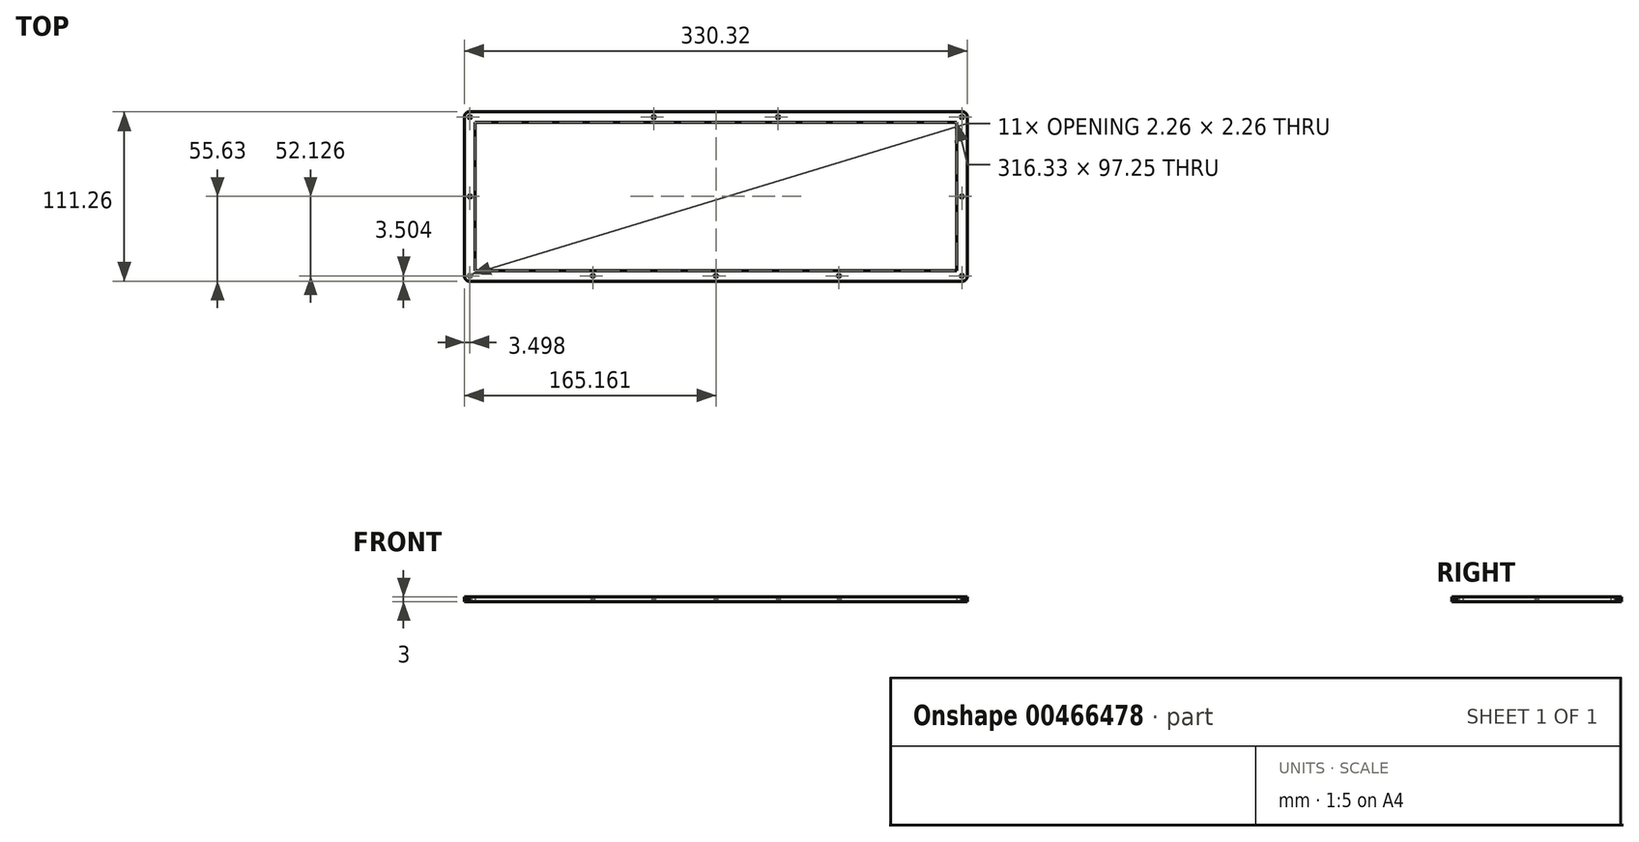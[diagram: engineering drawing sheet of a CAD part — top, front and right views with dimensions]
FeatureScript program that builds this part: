
annotation { "Feature Type Name" : "Feature", "Feature Type Description" : "" }
export const myFeature = defineFeature(function(context is Context, id is Id, definition is map)
    precondition{}
    {
        {
            var Q0;
            Q0=qCreatedBy(makeId("Top.planeOp"),FACE);
            var sketch = newSketch(context, id + "F0", { "sketchPlane" : qUnion([Q0])});
            skLineSegment(sketch, "E0", {"start": v(162.16, 55.62) * mm, "end": v(162.4, 55.62) * mm});
            skLineSegment(sketch, "E1", {"start": v(162.4, 55.62) * mm, "end": v(162.63, 55.59) * mm});
            skLineSegment(sketch, "E2", {"start": v(162.63, 55.59) * mm, "end": v(162.86, 55.54) * mm});
            skLineSegment(sketch, "E3", {"start": v(162.86, 55.54) * mm, "end": v(163.1, 55.48) * mm});
            skLineSegment(sketch, "E4", {"start": v(163.1, 55.48) * mm, "end": v(163.31, 55.4) * mm});
            skLineSegment(sketch, "E5", {"start": v(163.31, 55.4) * mm, "end": v(163.53, 55.3) * mm});
            skLineSegment(sketch, "E6", {"start": v(163.53, 55.3) * mm, "end": v(163.73, 55.18) * mm});
            skLineSegment(sketch, "E7", {"start": v(163.73, 55.18) * mm, "end": v(163.93, 55.05) * mm});
            skLineSegment(sketch, "E8", {"start": v(163.93, 55.05) * mm, "end": v(164.11, 54.9) * mm});
            skLineSegment(sketch, "E9", {"start": v(164.11, 54.9) * mm, "end": v(164.29, 54.75) * mm});
            skLineSegment(sketch, "E10", {"start": v(164.29, 54.75) * mm, "end": v(164.45, 54.57) * mm});
            skLineSegment(sketch, "E11", {"start": v(164.45, 54.57) * mm, "end": v(164.6, 54.39) * mm});
            skLineSegment(sketch, "E12", {"start": v(164.6, 54.39) * mm, "end": v(164.72, 54.2) * mm});
            skLineSegment(sketch, "E13", {"start": v(164.72, 54.2) * mm, "end": v(164.84, 53.99) * mm});
            skLineSegment(sketch, "E14", {"start": v(164.84, 53.99) * mm, "end": v(164.93, 53.77) * mm});
            skLineSegment(sketch, "E15", {"start": v(164.93, 53.77) * mm, "end": v(165.02, 53.55) * mm});
            skLineSegment(sketch, "E16", {"start": v(165.02, 53.55) * mm, "end": v(165.08, 53.33) * mm});
            skLineSegment(sketch, "E17", {"start": v(165.08, 53.33) * mm, "end": v(165.13, 53.1) * mm});
            skLineSegment(sketch, "E18", {"start": v(165.13, 53.1) * mm, "end": v(165.15, 52.86) * mm});
            skLineSegment(sketch, "E19", {"start": v(165.15, 52.86) * mm, "end": v(165.16, 52.62) * mm});
            skLineSegment(sketch, "E20", {"start": v(165.16, 52.62) * mm, "end": v(165.16, -52.63) * mm});
            skLineSegment(sketch, "E21", {"start": v(165.16, -52.63) * mm, "end": v(165.15, -52.86) * mm});
            skLineSegment(sketch, "E22", {"start": v(165.15, -52.86) * mm, "end": v(165.13, -53.1) * mm});
            skLineSegment(sketch, "E23", {"start": v(165.13, -53.1) * mm, "end": v(165.08, -53.33) * mm});
            skLineSegment(sketch, "E24", {"start": v(165.08, -53.33) * mm, "end": v(165.02, -53.55) * mm});
            skLineSegment(sketch, "E25", {"start": v(165.02, -53.55) * mm, "end": v(164.93, -53.77) * mm});
            skLineSegment(sketch, "E26", {"start": v(164.93, -53.77) * mm, "end": v(164.84, -53.99) * mm});
            skLineSegment(sketch, "E27", {"start": v(164.84, -53.99) * mm, "end": v(164.72, -54.2) * mm});
            skLineSegment(sketch, "E28", {"start": v(164.72, -54.2) * mm, "end": v(164.6, -54.39) * mm});
            skLineSegment(sketch, "E29", {"start": v(164.6, -54.39) * mm, "end": v(164.45, -54.57) * mm});
            skLineSegment(sketch, "E30", {"start": v(164.45, -54.57) * mm, "end": v(164.29, -54.75) * mm});
            skLineSegment(sketch, "E31", {"start": v(164.29, -54.75) * mm, "end": v(164.11, -54.9) * mm});
            skLineSegment(sketch, "E32", {"start": v(164.11, -54.9) * mm, "end": v(163.93, -55.05) * mm});
            skLineSegment(sketch, "E33", {"start": v(163.93, -55.05) * mm, "end": v(163.73, -55.18) * mm});
            skLineSegment(sketch, "E34", {"start": v(163.73, -55.18) * mm, "end": v(163.53, -55.3) * mm});
            skLineSegment(sketch, "E35", {"start": v(163.53, -55.3) * mm, "end": v(163.31, -55.4) * mm});
            skLineSegment(sketch, "E36", {"start": v(163.31, -55.4) * mm, "end": v(163.1, -55.48) * mm});
            skLineSegment(sketch, "E37", {"start": v(163.1, -55.48) * mm, "end": v(162.86, -55.54) * mm});
            skLineSegment(sketch, "E38", {"start": v(162.86, -55.54) * mm, "end": v(162.63, -55.59) * mm});
            skLineSegment(sketch, "E39", {"start": v(162.63, -55.59) * mm, "end": v(162.4, -55.62) * mm});
            skLineSegment(sketch, "E40", {"start": v(162.4, -55.62) * mm, "end": v(162.16, -55.63) * mm});
            skLineSegment(sketch, "E41", {"start": v(162.16, -55.63) * mm, "end": v(-162.16, -55.63) * mm});
            skLineSegment(sketch, "E42", {"start": v(-162.16, -55.63) * mm, "end": v(-162.4, -55.62) * mm});
            skLineSegment(sketch, "E43", {"start": v(-162.4, -55.62) * mm, "end": v(-162.63, -55.59) * mm});
            skLineSegment(sketch, "E44", {"start": v(-162.63, -55.59) * mm, "end": v(-162.86, -55.54) * mm});
            skLineSegment(sketch, "E45", {"start": v(-162.86, -55.54) * mm, "end": v(-163.09, -55.48) * mm});
            skLineSegment(sketch, "E46", {"start": v(-163.09, -55.48) * mm, "end": v(-163.31, -55.4) * mm});
            skLineSegment(sketch, "E47", {"start": v(-163.31, -55.4) * mm, "end": v(-163.52, -55.3) * mm});
            skLineSegment(sketch, "E48", {"start": v(-163.52, -55.3) * mm, "end": v(-163.73, -55.18) * mm});
            skLineSegment(sketch, "E49", {"start": v(-163.73, -55.18) * mm, "end": v(-163.93, -55.05) * mm});
            skLineSegment(sketch, "E50", {"start": v(-163.93, -55.05) * mm, "end": v(-164.11, -54.9) * mm});
            skLineSegment(sketch, "E51", {"start": v(-164.11, -54.9) * mm, "end": v(-164.28, -54.75) * mm});
            skLineSegment(sketch, "E52", {"start": v(-164.28, -54.75) * mm, "end": v(-164.44, -54.57) * mm});
            skLineSegment(sketch, "E53", {"start": v(-164.44, -54.57) * mm, "end": v(-164.6, -54.39) * mm});
            skLineSegment(sketch, "E54", {"start": v(-164.6, -54.39) * mm, "end": v(-164.72, -54.2) * mm});
            skLineSegment(sketch, "E55", {"start": v(-164.72, -54.2) * mm, "end": v(-164.84, -53.99) * mm});
            skLineSegment(sketch, "E56", {"start": v(-164.84, -53.99) * mm, "end": v(-164.93, -53.77) * mm});
            skLineSegment(sketch, "E57", {"start": v(-164.93, -53.77) * mm, "end": v(-165.02, -53.55) * mm});
            skLineSegment(sketch, "E58", {"start": v(-165.02, -53.55) * mm, "end": v(-165.08, -53.33) * mm});
            skLineSegment(sketch, "E59", {"start": v(-165.08, -53.33) * mm, "end": v(-165.13, -53.1) * mm});
            skLineSegment(sketch, "E60", {"start": v(-165.13, -53.1) * mm, "end": v(-165.15, -52.86) * mm});
            skLineSegment(sketch, "E61", {"start": v(-165.15, -52.86) * mm, "end": v(-165.16, -52.63) * mm});
            skLineSegment(sketch, "E62", {"start": v(-165.16, -52.63) * mm, "end": v(-165.16, 52.62) * mm});
            skLineSegment(sketch, "E63", {"start": v(-165.16, 52.62) * mm, "end": v(-165.15, 52.86) * mm});
            skLineSegment(sketch, "E64", {"start": v(-165.15, 52.86) * mm, "end": v(-165.13, 53.1) * mm});
            skLineSegment(sketch, "E65", {"start": v(-165.13, 53.1) * mm, "end": v(-165.08, 53.33) * mm});
            skLineSegment(sketch, "E66", {"start": v(-165.08, 53.33) * mm, "end": v(-165.02, 53.55) * mm});
            skLineSegment(sketch, "E67", {"start": v(-165.02, 53.55) * mm, "end": v(-164.93, 53.77) * mm});
            skLineSegment(sketch, "E68", {"start": v(-164.93, 53.77) * mm, "end": v(-164.84, 53.99) * mm});
            skLineSegment(sketch, "E69", {"start": v(-164.84, 53.99) * mm, "end": v(-164.72, 54.2) * mm});
            skLineSegment(sketch, "E70", {"start": v(-164.72, 54.2) * mm, "end": v(-164.6, 54.39) * mm});
            skLineSegment(sketch, "E71", {"start": v(-164.6, 54.39) * mm, "end": v(-164.44, 54.57) * mm});
            skLineSegment(sketch, "E72", {"start": v(-164.44, 54.57) * mm, "end": v(-164.28, 54.75) * mm});
            skLineSegment(sketch, "E73", {"start": v(-164.28, 54.75) * mm, "end": v(-164.11, 54.9) * mm});
            skLineSegment(sketch, "E74", {"start": v(-164.11, 54.9) * mm, "end": v(-163.93, 55.05) * mm});
            skLineSegment(sketch, "E75", {"start": v(-163.93, 55.05) * mm, "end": v(-163.73, 55.18) * mm});
            skLineSegment(sketch, "E76", {"start": v(-163.73, 55.18) * mm, "end": v(-163.52, 55.3) * mm});
            skLineSegment(sketch, "E77", {"start": v(-163.52, 55.3) * mm, "end": v(-163.31, 55.4) * mm});
            skLineSegment(sketch, "E78", {"start": v(-163.31, 55.4) * mm, "end": v(-163.09, 55.48) * mm});
            skLineSegment(sketch, "E79", {"start": v(-163.09, 55.48) * mm, "end": v(-162.86, 55.54) * mm});
            skLineSegment(sketch, "E80", {"start": v(-162.86, 55.54) * mm, "end": v(-162.63, 55.59) * mm});
            skLineSegment(sketch, "E81", {"start": v(-162.63, 55.59) * mm, "end": v(-162.4, 55.62) * mm});
            skLineSegment(sketch, "E82", {"start": v(-162.4, 55.62) * mm, "end": v(-162.16, 55.63) * mm});
            skLineSegment(sketch, "E83", {"start": v(-162.16, 55.63) * mm, "end": v(162.16, 55.62) * mm});
            skLineSegment(sketch, "E84", {"start": v(161.31, -51.05) * mm, "end": v(161, -51.21) * mm});
            skLineSegment(sketch, "E85", {"start": v(161, -51.21) * mm, "end": v(160.75, -51.46) * mm});
            skLineSegment(sketch, "E86", {"start": v(160.75, -51.46) * mm, "end": v(160.59, -51.78) * mm});
            skLineSegment(sketch, "E87", {"start": v(160.59, -51.78) * mm, "end": v(160.53, -52.13) * mm});
            skLineSegment(sketch, "E88", {"start": v(160.53, -52.13) * mm, "end": v(160.59, -52.48) * mm});
            skLineSegment(sketch, "E89", {"start": v(160.59, -52.48) * mm, "end": v(160.75, -52.79) * mm});
            skLineSegment(sketch, "E90", {"start": v(160.75, -52.79) * mm, "end": v(161, -53.04) * mm});
            skLineSegment(sketch, "E91", {"start": v(161, -53.04) * mm, "end": v(161.31, -53.2) * mm});
            skLineSegment(sketch, "E92", {"start": v(161.31, -53.2) * mm, "end": v(161.66, -53.26) * mm});
            skLineSegment(sketch, "E93", {"start": v(161.66, -53.26) * mm, "end": v(162.01, -53.2) * mm});
            skLineSegment(sketch, "E94", {"start": v(162.01, -53.2) * mm, "end": v(162.33, -53.04) * mm});
            skLineSegment(sketch, "E95", {"start": v(162.33, -53.04) * mm, "end": v(162.58, -52.79) * mm});
            skLineSegment(sketch, "E96", {"start": v(162.58, -52.79) * mm, "end": v(162.74, -52.48) * mm});
            skLineSegment(sketch, "E97", {"start": v(162.74, -52.48) * mm, "end": v(162.8, -52.13) * mm});
            skLineSegment(sketch, "E98", {"start": v(162.8, -52.13) * mm, "end": v(162.74, -51.78) * mm});
            skLineSegment(sketch, "E99", {"start": v(162.74, -51.78) * mm, "end": v(162.58, -51.46) * mm});
            skLineSegment(sketch, "E100", {"start": v(162.58, -51.46) * mm, "end": v(162.33, -51.21) * mm});
            skLineSegment(sketch, "E101", {"start": v(162.33, -51.21) * mm, "end": v(162.01, -51.05) * mm});
            skLineSegment(sketch, "E102", {"start": v(162.01, -51.05) * mm, "end": v(161.66, -51) * mm});
            skLineSegment(sketch, "E103", {"start": v(161.66, -51) * mm, "end": v(161.31, -51.05) * mm});
            skLineSegment(sketch, "E104", {"start": v(80.48, -51.05) * mm, "end": v(80.17, -51.21) * mm});
            skLineSegment(sketch, "E105", {"start": v(80.17, -51.21) * mm, "end": v(79.92, -51.46) * mm});
            skLineSegment(sketch, "E106", {"start": v(79.92, -51.46) * mm, "end": v(79.76, -51.78) * mm});
            skLineSegment(sketch, "E107", {"start": v(79.76, -51.78) * mm, "end": v(79.7, -52.13) * mm});
            skLineSegment(sketch, "E108", {"start": v(79.7, -52.13) * mm, "end": v(79.76, -52.48) * mm});
            skLineSegment(sketch, "E109", {"start": v(79.76, -52.48) * mm, "end": v(79.92, -52.79) * mm});
            skLineSegment(sketch, "E110", {"start": v(79.92, -52.79) * mm, "end": v(80.17, -53.04) * mm});
            skLineSegment(sketch, "E111", {"start": v(80.17, -53.04) * mm, "end": v(80.48, -53.2) * mm});
            skLineSegment(sketch, "E112", {"start": v(80.48, -53.2) * mm, "end": v(80.83, -53.26) * mm});
            skLineSegment(sketch, "E113", {"start": v(80.83, -53.26) * mm, "end": v(81.18, -53.2) * mm});
            skLineSegment(sketch, "E114", {"start": v(81.18, -53.2) * mm, "end": v(81.5, -53.04) * mm});
            skLineSegment(sketch, "E115", {"start": v(81.5, -53.04) * mm, "end": v(81.75, -52.79) * mm});
            skLineSegment(sketch, "E116", {"start": v(81.75, -52.79) * mm, "end": v(81.9, -52.48) * mm});
            skLineSegment(sketch, "E117", {"start": v(81.9, -52.48) * mm, "end": v(81.96, -52.13) * mm});
            skLineSegment(sketch, "E118", {"start": v(81.96, -52.13) * mm, "end": v(81.9, -51.78) * mm});
            skLineSegment(sketch, "E119", {"start": v(81.9, -51.78) * mm, "end": v(81.75, -51.46) * mm});
            skLineSegment(sketch, "E120", {"start": v(81.75, -51.46) * mm, "end": v(81.5, -51.21) * mm});
            skLineSegment(sketch, "E121", {"start": v(81.5, -51.21) * mm, "end": v(81.18, -51.05) * mm});
            skLineSegment(sketch, "E122", {"start": v(81.18, -51.05) * mm, "end": v(80.83, -51) * mm});
            skLineSegment(sketch, "E123", {"start": v(80.83, -51) * mm, "end": v(80.48, -51.05) * mm});
            skLineSegment(sketch, "E124", {"start": v(-0.35, -51.05) * mm, "end": v(-0.66, -51.21) * mm});
            skLineSegment(sketch, "E125", {"start": v(-0.66, -51.21) * mm, "end": v(-0.91, -51.46) * mm});
            skLineSegment(sketch, "E126", {"start": v(-0.91, -51.46) * mm, "end": v(-1.07, -51.78) * mm});
            skLineSegment(sketch, "E127", {"start": v(-1.07, -51.78) * mm, "end": v(-1.13, -52.13) * mm});
            skLineSegment(sketch, "E128", {"start": v(-1.13, -52.13) * mm, "end": v(-1.07, -52.48) * mm});
            skLineSegment(sketch, "E129", {"start": v(-1.07, -52.48) * mm, "end": v(-0.91, -52.79) * mm});
            skLineSegment(sketch, "E130", {"start": v(-0.91, -52.79) * mm, "end": v(-0.66, -53.04) * mm});
            skLineSegment(sketch, "E131", {"start": v(-0.66, -53.04) * mm, "end": v(-0.35, -53.2) * mm});
            skLineSegment(sketch, "E132", {"start": v(-0.35, -53.2) * mm, "end": v(0, -53.26) * mm});
            skLineSegment(sketch, "E133", {"start": v(0, -53.26) * mm, "end": v(0.35, -53.2) * mm});
            skLineSegment(sketch, "E134", {"start": v(0.35, -53.2) * mm, "end": v(0.67, -53.04) * mm});
            skLineSegment(sketch, "E135", {"start": v(0.67, -53.04) * mm, "end": v(0.92, -52.79) * mm});
            skLineSegment(sketch, "E136", {"start": v(0.92, -52.79) * mm, "end": v(1.07, -52.48) * mm});
            skLineSegment(sketch, "E137", {"start": v(1.07, -52.48) * mm, "end": v(1.13, -52.13) * mm});
            skLineSegment(sketch, "E138", {"start": v(1.13, -52.13) * mm, "end": v(1.07, -51.78) * mm});
            skLineSegment(sketch, "E139", {"start": v(1.07, -51.78) * mm, "end": v(0.92, -51.46) * mm});
            skLineSegment(sketch, "E140", {"start": v(0.92, -51.46) * mm, "end": v(0.67, -51.21) * mm});
            skLineSegment(sketch, "E141", {"start": v(0.67, -51.21) * mm, "end": v(0.35, -51.05) * mm});
            skLineSegment(sketch, "E142", {"start": v(0.35, -51.05) * mm, "end": v(0, -51) * mm});
            skLineSegment(sketch, "E143", {"start": v(0, -51) * mm, "end": v(-0.35, -51.05) * mm});
            skLineSegment(sketch, "E144", {"start": v(-81.18, -51.05) * mm, "end": v(-81.5, -51.21) * mm});
            skLineSegment(sketch, "E145", {"start": v(-81.5, -51.21) * mm, "end": v(-81.75, -51.46) * mm});
            skLineSegment(sketch, "E146", {"start": v(-81.75, -51.46) * mm, "end": v(-81.9, -51.78) * mm});
            skLineSegment(sketch, "E147", {"start": v(-81.9, -51.78) * mm, "end": v(-81.96, -52.13) * mm});
            skLineSegment(sketch, "E148", {"start": v(-81.96, -52.13) * mm, "end": v(-81.9, -52.48) * mm});
            skLineSegment(sketch, "E149", {"start": v(-81.9, -52.48) * mm, "end": v(-81.75, -52.79) * mm});
            skLineSegment(sketch, "E150", {"start": v(-81.75, -52.79) * mm, "end": v(-81.5, -53.04) * mm});
            skLineSegment(sketch, "E151", {"start": v(-81.5, -53.04) * mm, "end": v(-81.18, -53.2) * mm});
            skLineSegment(sketch, "E152", {"start": v(-81.18, -53.2) * mm, "end": v(-80.83, -53.26) * mm});
            skLineSegment(sketch, "E153", {"start": v(-80.83, -53.26) * mm, "end": v(-80.48, -53.2) * mm});
            skLineSegment(sketch, "E154", {"start": v(-80.48, -53.2) * mm, "end": v(-80.17, -53.04) * mm});
            skLineSegment(sketch, "E155", {"start": v(-80.17, -53.04) * mm, "end": v(-79.92, -52.79) * mm});
            skLineSegment(sketch, "E156", {"start": v(-79.92, -52.79) * mm, "end": v(-79.76, -52.48) * mm});
            skLineSegment(sketch, "E157", {"start": v(-79.76, -52.48) * mm, "end": v(-79.7, -52.13) * mm});
            skLineSegment(sketch, "E158", {"start": v(-79.7, -52.13) * mm, "end": v(-79.76, -51.78) * mm});
            skLineSegment(sketch, "E159", {"start": v(-79.76, -51.78) * mm, "end": v(-79.92, -51.46) * mm});
            skLineSegment(sketch, "E160", {"start": v(-79.92, -51.46) * mm, "end": v(-80.17, -51.21) * mm});
            skLineSegment(sketch, "E161", {"start": v(-80.17, -51.21) * mm, "end": v(-80.48, -51.05) * mm});
            skLineSegment(sketch, "E162", {"start": v(-80.48, -51.05) * mm, "end": v(-80.83, -51) * mm});
            skLineSegment(sketch, "E163", {"start": v(-80.83, -51) * mm, "end": v(-81.18, -51.05) * mm});
            skLineSegment(sketch, "E164", {"start": v(-162.01, -51.05) * mm, "end": v(-162.33, -51.21) * mm});
            skLineSegment(sketch, "E165", {"start": v(-162.33, -51.21) * mm, "end": v(-162.58, -51.46) * mm});
            skLineSegment(sketch, "E166", {"start": v(-162.58, -51.46) * mm, "end": v(-162.74, -51.78) * mm});
            skLineSegment(sketch, "E167", {"start": v(-162.74, -51.78) * mm, "end": v(-162.8, -52.13) * mm});
            skLineSegment(sketch, "E168", {"start": v(-162.8, -52.13) * mm, "end": v(-162.74, -52.48) * mm});
            skLineSegment(sketch, "E169", {"start": v(-162.74, -52.48) * mm, "end": v(-162.58, -52.79) * mm});
            skLineSegment(sketch, "E170", {"start": v(-162.58, -52.79) * mm, "end": v(-162.33, -53.04) * mm});
            skLineSegment(sketch, "E171", {"start": v(-162.33, -53.04) * mm, "end": v(-162.01, -53.2) * mm});
            skLineSegment(sketch, "E172", {"start": v(-162.01, -53.2) * mm, "end": v(-161.66, -53.26) * mm});
            skLineSegment(sketch, "E173", {"start": v(-161.66, -53.26) * mm, "end": v(-161.31, -53.2) * mm});
            skLineSegment(sketch, "E174", {"start": v(-161.31, -53.2) * mm, "end": v(-161, -53.04) * mm});
            skLineSegment(sketch, "E175", {"start": v(-161, -53.04) * mm, "end": v(-160.75, -52.79) * mm});
            skLineSegment(sketch, "E176", {"start": v(-160.75, -52.79) * mm, "end": v(-160.59, -52.48) * mm});
            skLineSegment(sketch, "E177", {"start": v(-160.59, -52.48) * mm, "end": v(-160.53, -52.13) * mm});
            skLineSegment(sketch, "E178", {"start": v(-160.53, -52.13) * mm, "end": v(-160.59, -51.78) * mm});
            skLineSegment(sketch, "E179", {"start": v(-160.59, -51.78) * mm, "end": v(-160.75, -51.46) * mm});
            skLineSegment(sketch, "E180", {"start": v(-160.75, -51.46) * mm, "end": v(-161, -51.21) * mm});
            skLineSegment(sketch, "E181", {"start": v(-161, -51.21) * mm, "end": v(-161.31, -51.05) * mm});
            skLineSegment(sketch, "E182", {"start": v(-161.31, -51.05) * mm, "end": v(-161.66, -51) * mm});
            skLineSegment(sketch, "E183", {"start": v(-161.66, -51) * mm, "end": v(-162.01, -51.05) * mm});
            skLineSegment(sketch, "E184", {"start": v(-158.16, 48.62) * mm, "end": v(158.16, 48.62) * mm});
            skLineSegment(sketch, "E185", {"start": v(158.16, 48.62) * mm, "end": v(158.16, -48.63) * mm});
            skLineSegment(sketch, "E186", {"start": v(158.16, -48.63) * mm, "end": v(-158.16, -48.63) * mm});
            skLineSegment(sketch, "E187", {"start": v(-158.16, -48.63) * mm, "end": v(-158.16, 48.62) * mm});
            skLineSegment(sketch, "E188", {"start": v(161.31, 1.08) * mm, "end": v(161, 0.91) * mm});
            skLineSegment(sketch, "E189", {"start": v(161, 0.91) * mm, "end": v(160.75, 0.66) * mm});
            skLineSegment(sketch, "E190", {"start": v(160.75, 0.66) * mm, "end": v(160.59, 0.35) * mm});
            skLineSegment(sketch, "E191", {"start": v(160.59, 0.35) * mm, "end": v(160.53, 0) * mm});
            skLineSegment(sketch, "E192", {"start": v(160.53, 0) * mm, "end": v(160.59, -0.35) * mm});
            skLineSegment(sketch, "E193", {"start": v(160.59, -0.35) * mm, "end": v(160.75, -0.66) * mm});
            skLineSegment(sketch, "E194", {"start": v(160.75, -0.66) * mm, "end": v(161, -0.91) * mm});
            skLineSegment(sketch, "E195", {"start": v(161, -0.91) * mm, "end": v(161.31, -1.07) * mm});
            skLineSegment(sketch, "E196", {"start": v(161.31, -1.07) * mm, "end": v(161.66, -1.13) * mm});
            skLineSegment(sketch, "E197", {"start": v(161.66, -1.13) * mm, "end": v(162.01, -1.07) * mm});
            skLineSegment(sketch, "E198", {"start": v(162.01, -1.07) * mm, "end": v(162.33, -0.91) * mm});
            skLineSegment(sketch, "E199", {"start": v(162.33, -0.91) * mm, "end": v(162.58, -0.66) * mm});
            skLineSegment(sketch, "E200", {"start": v(162.58, -0.66) * mm, "end": v(162.74, -0.35) * mm});
            skLineSegment(sketch, "E201", {"start": v(162.74, -0.35) * mm, "end": v(162.8, 0) * mm});
            skLineSegment(sketch, "E202", {"start": v(162.8, 0) * mm, "end": v(162.74, 0.35) * mm});
            skLineSegment(sketch, "E203", {"start": v(162.74, 0.35) * mm, "end": v(162.58, 0.66) * mm});
            skLineSegment(sketch, "E204", {"start": v(162.58, 0.66) * mm, "end": v(162.33, 0.91) * mm});
            skLineSegment(sketch, "E205", {"start": v(162.33, 0.91) * mm, "end": v(162.01, 1.08) * mm});
            skLineSegment(sketch, "E206", {"start": v(162.01, 1.08) * mm, "end": v(161.66, 1.13) * mm});
            skLineSegment(sketch, "E207", {"start": v(161.66, 1.13) * mm, "end": v(161.31, 1.08) * mm});
            skLineSegment(sketch, "E208", {"start": v(-162.01, 1.08) * mm, "end": v(-162.33, 0.91) * mm});
            skLineSegment(sketch, "E209", {"start": v(-162.33, 0.91) * mm, "end": v(-162.58, 0.66) * mm});
            skLineSegment(sketch, "E210", {"start": v(-162.58, 0.66) * mm, "end": v(-162.74, 0.35) * mm});
            skLineSegment(sketch, "E211", {"start": v(-162.74, 0.35) * mm, "end": v(-162.8, 0) * mm});
            skLineSegment(sketch, "E212", {"start": v(-162.8, 0) * mm, "end": v(-162.74, -0.35) * mm});
            skLineSegment(sketch, "E213", {"start": v(-162.74, -0.35) * mm, "end": v(-162.58, -0.66) * mm});
            skLineSegment(sketch, "E214", {"start": v(-162.58, -0.66) * mm, "end": v(-162.33, -0.91) * mm});
            skLineSegment(sketch, "E215", {"start": v(-162.33, -0.91) * mm, "end": v(-162.01, -1.07) * mm});
            skLineSegment(sketch, "E216", {"start": v(-162.01, -1.07) * mm, "end": v(-161.66, -1.13) * mm});
            skLineSegment(sketch, "E217", {"start": v(-161.66, -1.13) * mm, "end": v(-161.31, -1.07) * mm});
            skLineSegment(sketch, "E218", {"start": v(-161.31, -1.07) * mm, "end": v(-161, -0.91) * mm});
            skLineSegment(sketch, "E219", {"start": v(-161, -0.91) * mm, "end": v(-160.75, -0.66) * mm});
            skLineSegment(sketch, "E220", {"start": v(-160.75, -0.66) * mm, "end": v(-160.59, -0.35) * mm});
            skLineSegment(sketch, "E221", {"start": v(-160.59, -0.35) * mm, "end": v(-160.53, 0) * mm});
            skLineSegment(sketch, "E222", {"start": v(-160.53, 0) * mm, "end": v(-160.59, 0.35) * mm});
            skLineSegment(sketch, "E223", {"start": v(-160.59, 0.35) * mm, "end": v(-160.75, 0.66) * mm});
            skLineSegment(sketch, "E224", {"start": v(-160.75, 0.66) * mm, "end": v(-161, 0.91) * mm});
            skLineSegment(sketch, "E225", {"start": v(-161, 0.91) * mm, "end": v(-161.31, 1.08) * mm});
            skLineSegment(sketch, "E226", {"start": v(-161.31, 1.08) * mm, "end": v(-161.66, 1.13) * mm});
            skLineSegment(sketch, "E227", {"start": v(-161.66, 1.13) * mm, "end": v(-162.01, 1.08) * mm});
            skLineSegment(sketch, "E228", {"start": v(-41.18, 53.2) * mm, "end": v(-41.5, 53.04) * mm});
            skLineSegment(sketch, "E229", {"start": v(-41.5, 53.04) * mm, "end": v(-41.75, 52.8) * mm});
            skLineSegment(sketch, "E230", {"start": v(-41.75, 52.8) * mm, "end": v(-41.9, 52.47) * mm});
            skLineSegment(sketch, "E231", {"start": v(-41.9, 52.47) * mm, "end": v(-41.96, 52.12) * mm});
            skLineSegment(sketch, "E232", {"start": v(-41.96, 52.12) * mm, "end": v(-41.9, 51.78) * mm});
            skLineSegment(sketch, "E233", {"start": v(-41.9, 51.78) * mm, "end": v(-41.75, 51.46) * mm});
            skLineSegment(sketch, "E234", {"start": v(-41.75, 51.46) * mm, "end": v(-41.5, 51.21) * mm});
            skLineSegment(sketch, "E235", {"start": v(-41.5, 51.21) * mm, "end": v(-41.18, 51.05) * mm});
            skLineSegment(sketch, "E236", {"start": v(-41.18, 51.05) * mm, "end": v(-40.83, 51) * mm});
            skLineSegment(sketch, "E237", {"start": v(-40.83, 51) * mm, "end": v(-40.48, 51.05) * mm});
            skLineSegment(sketch, "E238", {"start": v(-40.48, 51.05) * mm, "end": v(-40.17, 51.21) * mm});
            skLineSegment(sketch, "E239", {"start": v(-40.17, 51.21) * mm, "end": v(-39.92, 51.46) * mm});
            skLineSegment(sketch, "E240", {"start": v(-39.92, 51.46) * mm, "end": v(-39.76, 51.78) * mm});
            skLineSegment(sketch, "E241", {"start": v(-39.76, 51.78) * mm, "end": v(-39.7, 52.12) * mm});
            skLineSegment(sketch, "E242", {"start": v(-39.7, 52.12) * mm, "end": v(-39.76, 52.47) * mm});
            skLineSegment(sketch, "E243", {"start": v(-39.76, 52.47) * mm, "end": v(-39.92, 52.8) * mm});
            skLineSegment(sketch, "E244", {"start": v(-39.92, 52.8) * mm, "end": v(-40.17, 53.04) * mm});
            skLineSegment(sketch, "E245", {"start": v(-40.17, 53.04) * mm, "end": v(-40.48, 53.2) * mm});
            skLineSegment(sketch, "E246", {"start": v(-40.48, 53.2) * mm, "end": v(-40.83, 53.26) * mm});
            skLineSegment(sketch, "E247", {"start": v(-40.83, 53.26) * mm, "end": v(-41.18, 53.2) * mm});
            skLineSegment(sketch, "E248", {"start": v(40.48, 53.2) * mm, "end": v(40.17, 53.04) * mm});
            skLineSegment(sketch, "E249", {"start": v(40.17, 53.04) * mm, "end": v(39.92, 52.8) * mm});
            skLineSegment(sketch, "E250", {"start": v(39.92, 52.8) * mm, "end": v(39.76, 52.47) * mm});
            skLineSegment(sketch, "E251", {"start": v(39.76, 52.47) * mm, "end": v(39.7, 52.12) * mm});
            skLineSegment(sketch, "E252", {"start": v(39.7, 52.12) * mm, "end": v(39.76, 51.78) * mm});
            skLineSegment(sketch, "E253", {"start": v(39.76, 51.78) * mm, "end": v(39.92, 51.46) * mm});
            skLineSegment(sketch, "E254", {"start": v(39.92, 51.46) * mm, "end": v(40.17, 51.21) * mm});
            skLineSegment(sketch, "E255", {"start": v(40.17, 51.21) * mm, "end": v(40.48, 51.05) * mm});
            skLineSegment(sketch, "E256", {"start": v(40.48, 51.05) * mm, "end": v(40.83, 51) * mm});
            skLineSegment(sketch, "E257", {"start": v(40.83, 51) * mm, "end": v(41.18, 51.05) * mm});
            skLineSegment(sketch, "E258", {"start": v(41.18, 51.05) * mm, "end": v(41.5, 51.21) * mm});
            skLineSegment(sketch, "E259", {"start": v(41.5, 51.21) * mm, "end": v(41.75, 51.46) * mm});
            skLineSegment(sketch, "E260", {"start": v(41.75, 51.46) * mm, "end": v(41.9, 51.78) * mm});
            skLineSegment(sketch, "E261", {"start": v(41.9, 51.78) * mm, "end": v(41.96, 52.12) * mm});
            skLineSegment(sketch, "E262", {"start": v(41.96, 52.12) * mm, "end": v(41.9, 52.47) * mm});
            skLineSegment(sketch, "E263", {"start": v(41.9, 52.47) * mm, "end": v(41.75, 52.8) * mm});
            skLineSegment(sketch, "E264", {"start": v(41.75, 52.8) * mm, "end": v(41.5, 53.04) * mm});
            skLineSegment(sketch, "E265", {"start": v(41.5, 53.04) * mm, "end": v(41.18, 53.2) * mm});
            skLineSegment(sketch, "E266", {"start": v(41.18, 53.2) * mm, "end": v(40.83, 53.26) * mm});
            skLineSegment(sketch, "E267", {"start": v(40.83, 53.26) * mm, "end": v(40.48, 53.2) * mm});
            skLineSegment(sketch, "E268", {"start": v(161.31, 53.2) * mm, "end": v(161, 53.04) * mm});
            skLineSegment(sketch, "E269", {"start": v(161, 53.04) * mm, "end": v(160.75, 52.8) * mm});
            skLineSegment(sketch, "E270", {"start": v(160.75, 52.8) * mm, "end": v(160.59, 52.47) * mm});
            skLineSegment(sketch, "E271", {"start": v(160.59, 52.47) * mm, "end": v(160.53, 52.12) * mm});
            skLineSegment(sketch, "E272", {"start": v(160.53, 52.12) * mm, "end": v(160.59, 51.78) * mm});
            skLineSegment(sketch, "E273", {"start": v(160.59, 51.78) * mm, "end": v(160.75, 51.46) * mm});
            skLineSegment(sketch, "E274", {"start": v(160.75, 51.46) * mm, "end": v(161, 51.21) * mm});
            skLineSegment(sketch, "E275", {"start": v(161, 51.21) * mm, "end": v(161.31, 51.05) * mm});
            skLineSegment(sketch, "E276", {"start": v(161.31, 51.05) * mm, "end": v(161.66, 51) * mm});
            skLineSegment(sketch, "E277", {"start": v(161.66, 51) * mm, "end": v(162.01, 51.05) * mm});
            skLineSegment(sketch, "E278", {"start": v(162.01, 51.05) * mm, "end": v(162.33, 51.21) * mm});
            skLineSegment(sketch, "E279", {"start": v(162.33, 51.21) * mm, "end": v(162.58, 51.46) * mm});
            skLineSegment(sketch, "E280", {"start": v(162.58, 51.46) * mm, "end": v(162.74, 51.78) * mm});
            skLineSegment(sketch, "E281", {"start": v(162.74, 51.78) * mm, "end": v(162.8, 52.12) * mm});
            skLineSegment(sketch, "E282", {"start": v(162.8, 52.12) * mm, "end": v(162.74, 52.47) * mm});
            skLineSegment(sketch, "E283", {"start": v(162.74, 52.47) * mm, "end": v(162.58, 52.8) * mm});
            skLineSegment(sketch, "E284", {"start": v(162.58, 52.8) * mm, "end": v(162.33, 53.04) * mm});
            skLineSegment(sketch, "E285", {"start": v(162.33, 53.04) * mm, "end": v(162.01, 53.2) * mm});
            skLineSegment(sketch, "E286", {"start": v(162.01, 53.2) * mm, "end": v(161.66, 53.26) * mm});
            skLineSegment(sketch, "E287", {"start": v(161.66, 53.26) * mm, "end": v(161.31, 53.2) * mm});
            skLineSegment(sketch, "E288", {"start": v(-162.01, 53.2) * mm, "end": v(-162.33, 53.04) * mm});
            skLineSegment(sketch, "E289", {"start": v(-162.33, 53.04) * mm, "end": v(-162.58, 52.8) * mm});
            skLineSegment(sketch, "E290", {"start": v(-162.58, 52.8) * mm, "end": v(-162.74, 52.47) * mm});
            skLineSegment(sketch, "E291", {"start": v(-162.74, 52.47) * mm, "end": v(-162.8, 52.12) * mm});
            skLineSegment(sketch, "E292", {"start": v(-162.8, 52.12) * mm, "end": v(-162.74, 51.78) * mm});
            skLineSegment(sketch, "E293", {"start": v(-162.74, 51.78) * mm, "end": v(-162.58, 51.46) * mm});
            skLineSegment(sketch, "E294", {"start": v(-162.58, 51.46) * mm, "end": v(-162.33, 51.21) * mm});
            skLineSegment(sketch, "E295", {"start": v(-162.33, 51.21) * mm, "end": v(-162.01, 51.05) * mm});
            skLineSegment(sketch, "E296", {"start": v(-162.01, 51.05) * mm, "end": v(-161.66, 51) * mm});
            skLineSegment(sketch, "E297", {"start": v(-161.66, 51) * mm, "end": v(-161.31, 51.05) * mm});
            skLineSegment(sketch, "E298", {"start": v(-161.31, 51.05) * mm, "end": v(-161, 51.21) * mm});
            skLineSegment(sketch, "E299", {"start": v(-161, 51.21) * mm, "end": v(-160.75, 51.46) * mm});
            skLineSegment(sketch, "E300", {"start": v(-160.75, 51.46) * mm, "end": v(-160.59, 51.78) * mm});
            skLineSegment(sketch, "E301", {"start": v(-160.59, 51.78) * mm, "end": v(-160.53, 52.12) * mm});
            skLineSegment(sketch, "E302", {"start": v(-160.53, 52.12) * mm, "end": v(-160.59, 52.47) * mm});
            skLineSegment(sketch, "E303", {"start": v(-160.59, 52.47) * mm, "end": v(-160.75, 52.8) * mm});
            skLineSegment(sketch, "E304", {"start": v(-160.75, 52.8) * mm, "end": v(-161, 53.04) * mm});
            skLineSegment(sketch, "E305", {"start": v(-161, 53.04) * mm, "end": v(-161.31, 53.2) * mm});
            skLineSegment(sketch, "E306", {"start": v(-161.31, 53.2) * mm, "end": v(-161.66, 53.26) * mm});
            skLineSegment(sketch, "E307", {"start": v(-161.66, 53.26) * mm, "end": v(-162.01, 53.2) * mm});
            skSolve(sketch);
        }
        {
            var Q0;
            Q0=qSketchRegion(id+"F0",true);
            extrude(context, id + "F1", {"entities" : qUnion([Q0]), "depth" : 3 * mm});
        }
    });
